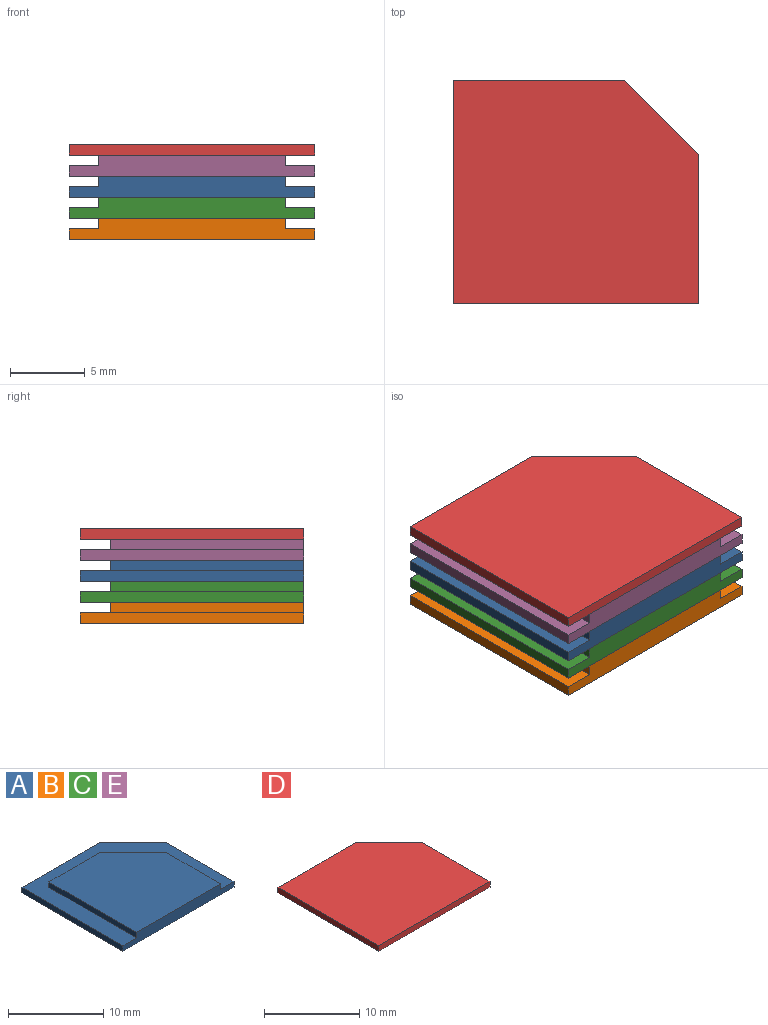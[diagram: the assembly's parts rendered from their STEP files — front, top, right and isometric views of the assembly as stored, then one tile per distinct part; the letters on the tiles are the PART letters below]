
ASSEMBLY  parts=5 mates=4
PART A: 12 faces, bbox 16.5x15x1.4 mm
  f0: plane 16.5x15mm, normal (0,0,1), area 85mm2, adj f1,f2,f3,f4,f6,f7,f8,f10
  f1: plane 16.5x1.42mm, normal (0,-1,0), area 20.5mm2, adj f0,f2,f4,f5,f6,f8,f9
  f2: plane 10x0.71mm, normal (1,0,0), area 7.1mm2, adj f0,f1,f5,f10
  f3: plane 11.5x0.71mm, normal (0,1,0), area 8.1mm2, adj f0,f4,f5,f10
  f4: plane 15x0.71mm, normal (-1,0,0), area 10.6mm2, adj f0,f1,f3,f5
  f5: plane 16.5x15mm, normal (0,0,-1), area 235mm2, adj f1,f2,f3,f4,f10
  f6: plane 8x0.71mm, normal (1,0,0), area 5.7mm2, adj f0,f1,f9,f11
  f7: plane 7.5x0.71mm, normal (0,1,0), area 5.3mm2, adj f0,f8,f9,f11
  f8: plane 13x0.71mm, normal (-1,0,0), area 9.2mm2, adj f0,f1,f7,f9
  f9: plane 13x12.5mm, normal (0,0,1), area 150mm2, adj f1,f6,f7,f8,f11
  f10: plane 5x5mm, normal (0.71,0.71,0), area 5mm2, adj f0,f2,f3,f5
  f11: plane 5x5mm, normal (0.71,0.71,0), area 5mm2, adj f0,f6,f7,f9
PART B: same geometry as A
PART C: same geometry as A
PART D: 7 faces, bbox 16.5x15x0.7 mm
  f0: plane 11.5x0.71mm, normal (0,1,0), area 8.1mm2, adj f1,f4,f5,f6
  f1: plane 5x5mm, normal (0.71,0.71,0), area 5mm2, adj f0,f2,f5,f6
  f2: plane 10x0.71mm, normal (1,0,0), area 7.1mm2, adj f1,f3,f5,f6
  f3: plane 16.5x0.71mm, normal (0,-1,0), area 11.7mm2, adj f2,f4,f5,f6
  f4: plane 15x0.71mm, normal (-1,0,0), area 10.6mm2, adj f0,f3,f5,f6
  f5: plane 16.5x15mm, normal (0,0,-1), area 235mm2, adj f0,f1,f2,f3,f4
  f6: plane 16.5x15mm, normal (0,0,1), area 235mm2, adj f0,f1,f2,f3,f4
PART E: same geometry as A
PLACE A t=(0.35,0.31,3.54)mm
PLACE B t=(0.35,0.31,0.71)mm
PLACE C t=(0.35,0.31,2.12)mm
PLACE D t=(0.35,0.31,7.08)mm
PLACE E t=(0.35,0.31,4.95)mm
MATE fastened E.f5 <-> A.f9  axis (0,0,-1) through (0.35,-7.19,4.25)mm
MATE fastened A.f5 <-> C.f9  axis (0,0,-1) through (0.35,-7.19,2.83)mm
MATE fastened D.f5 <-> E.f9  axis (0,0,-1) through (0.35,-7.19,5.66)mm
MATE fastened C.f5 <-> B.f9  axis (0,0,-1) through (0.35,-7.19,1.42)mm
